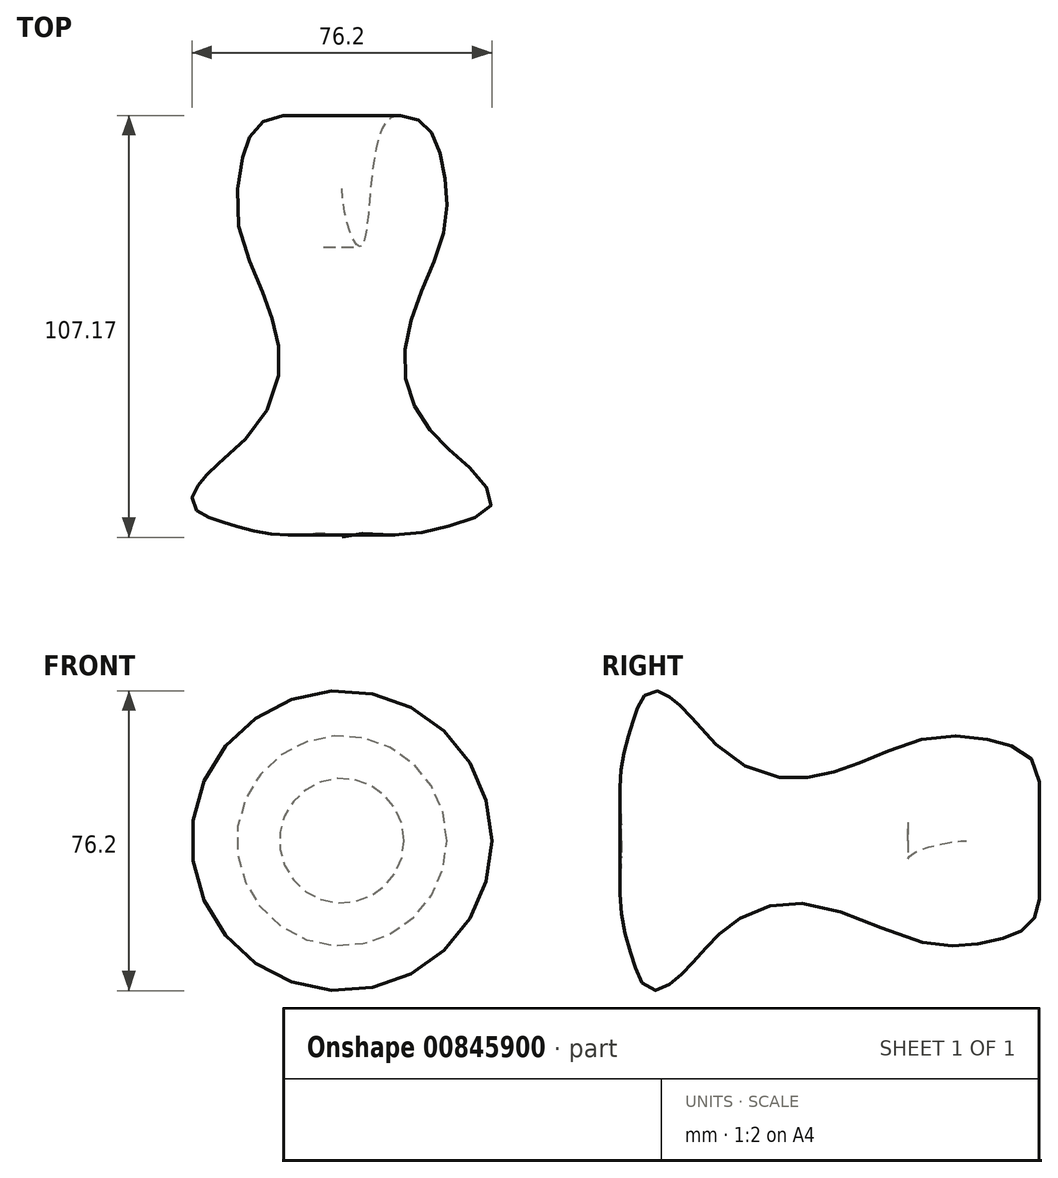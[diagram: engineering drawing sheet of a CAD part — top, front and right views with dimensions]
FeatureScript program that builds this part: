
annotation { "Feature Type Name" : "Feature", "Feature Type Description" : "" }
export const myFeature = defineFeature(function(context is Context, id is Id, definition is map)
    precondition{}
    {
        {
            var Q0;
            Q0=qCreatedBy(makeId("Top.planeOp"),FACE);
            var sketch = newSketch(context, id + "F0", { "sketchPlane" : qUnion([Q0])});
            skLineSegment(sketch, "E0", {"start": v(0, 76.6) * mm, "end": v(0, -76.4) * mm});
            skFitSpline(sketch, "E1", {"points": [v(0, 26.7) * mm, v(10.86, 46.83) * mm, v(19.1, 48.74) * mm, v(26.27, 46.52) * mm, v(30.58, 42.22) * mm, v(35.39, 15.24) * mm, v(29.1, 0) * mm, v(25.04, -17.28) * mm, v(31.32, -32.8) * mm, v(41.85, -41.67) * mm, v(49.43, -54.79) * mm, v(40.37, -66.8) * mm, v(1.39, -69.94) * mm, v(0, -65.14) * mm, v(13.4, -64.58) * mm, v(29.29, -61.62) * mm, v(37.97, -56.82) * mm, v(33.35, -48.32) * mm, v(22.45, -37.97) * mm, v(15.98, -23) * mm, v(19.12, -5.45) * mm, v(25.96, 12.84) * mm, v(25.96, 27.62) * mm, v(22.45, 38.16) * mm, v(17.28, 41.67) * mm, v(10.36, 39.02) * mm, v(4.97, 8.75) * mm, v(0, 26.7) * mm]});
            skSolve(sketch);
        }
        {
            var Q0;
            {var subQ0=sQuery(id+"F0.wireOp",EDGE,"E1");var subQ1=sQuery(id+"F0.wireOp",EDGE,"E0");var subQ2=makeQuery(id+"F0.imprint","INTERSECT",VERTEX,{"disambiguationData":[OD(0.0)],"derivedFrom":[subQ1,subQ0]});Q0=makeQuery(id+"F0.imprint","IMPRINT",FACE,{"disambiguationData":[TD([[makeQuery(id+"F0.imprint","IMPRINT",EDGE,{"disambiguationData":[TD([[subQ2,-1.0]])],"derivedFrom":subQ1}),1.0]])]});}
            var Q1;
            Q1=sQuery(id+"F0.wireOp",EDGE,"E0");
            revolve(context, id + "F1", {"surfaceOperationType" : NewSurfaceOperationType.NEW, "entities" : qUnion([Q0]), "axis" : qUnion([Q1]), "revolveType" : RevolveType.FULL});
        }
        {
            var Q0;
            Q0=qCreatedBy(makeId("Top.planeOp"),FACE);
            var sketch = newSketch(context, id + "F2", { "sketchPlane" : qUnion([Q0])});
            skFitSpline(sketch, "E2", {"points": [v(32.33, 12.66) * mm, v(55.23, 3.54) * mm, v(60.37, -15.85) * mm, v(33.96, -39.93) * mm], "startDerivative": vector(80.86, -17.38) * mm, "endDerivative": vector(-90.17, -57.95) * mm});
            skSolve(sketch);
        }
        {
            var Q0;
            Q0=sQuery(id+"F2.wireOp",VERTEX,"E2.end");
            var Q1;
            Q1=sQuery(id+"F2.wireOp",EDGE,"E2");
            cPlane(context, id + "F3", {"entities" : qUnion([Q0, Q1]), "cplaneType" : CPlaneType.CURVE_POINT, "offset" : 25.4 * mm, "width" : 152.4 * mm, "height" : 152.4 * mm});
        }
        {
            var Q0;
            Q0=qCreatedBy(id+"F3.planeOp",FACE);
            var sketch = newSketch(context, id + "F4", { "sketchPlane" : qUnion([Q0])});
            skCircle(sketch, "E3", {"center": v(51.85, 0) * mm, "radius": 3.8 * mm});
            skSolve(sketch);
        }
    });
